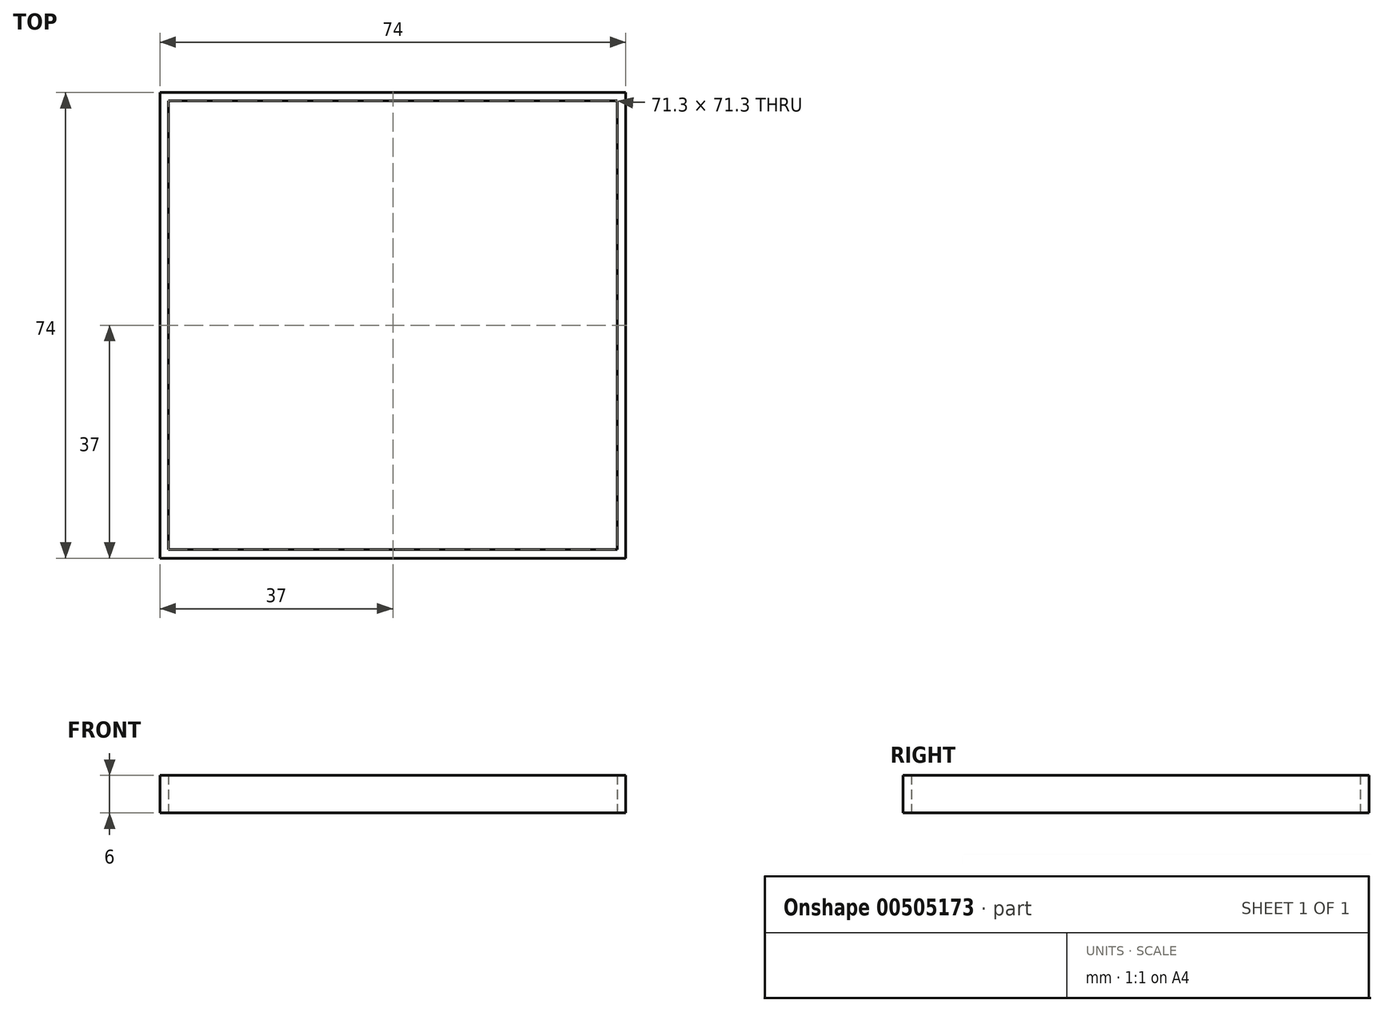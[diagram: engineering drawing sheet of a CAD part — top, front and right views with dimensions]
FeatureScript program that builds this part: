
annotation { "Feature Type Name" : "Feature", "Feature Type Description" : "" }
export const myFeature = defineFeature(function(context is Context, id is Id, definition is map)
    precondition{}
    {
        {
            var Q0;
            Q0=qCreatedBy(makeId("Top.planeOp"),FACE);
            var sketch = newSketch(context, id + "F0", { "sketchPlane" : qUnion([Q0])});
            skLineSegment(sketch, "E0.bottom", {"start": v(37, -37) * mm, "end": v(-37, -37) * mm});
            skLineSegment(sketch, "E0.top", {"start": v(37, 37) * mm, "end": v(-37, 37) * mm});
            skLineSegment(sketch, "E0.left", {"start": v(37, -37) * mm, "end": v(37, 37) * mm});
            skLineSegment(sketch, "E0.right", {"start": v(-37, -37) * mm, "end": v(-37, 37) * mm});
            skPoint(sketch, "E0.middle", {"position": v(0, 0) * mm});
            skLineSegment(sketch, "E1.bottom", {"start": v(35.65, -35.65) * mm, "end": v(-35.65, -35.65) * mm});
            skLineSegment(sketch, "E1.top", {"start": v(35.65, 35.65) * mm, "end": v(-35.65, 35.65) * mm});
            skLineSegment(sketch, "E1.left", {"start": v(35.65, -35.65) * mm, "end": v(35.65, 35.65) * mm});
            skLineSegment(sketch, "E1.right", {"start": v(-35.65, -35.65) * mm, "end": v(-35.65, 35.65) * mm});
            skSolve(sketch);
        }
        {
            var Q0;
            Q0 = qSketchRegion(id + "F0", true);
            extrude(context, id + "F1", {"entities" : qUnion([Q0]), "depth" : 6 * mm});
        }
    });
